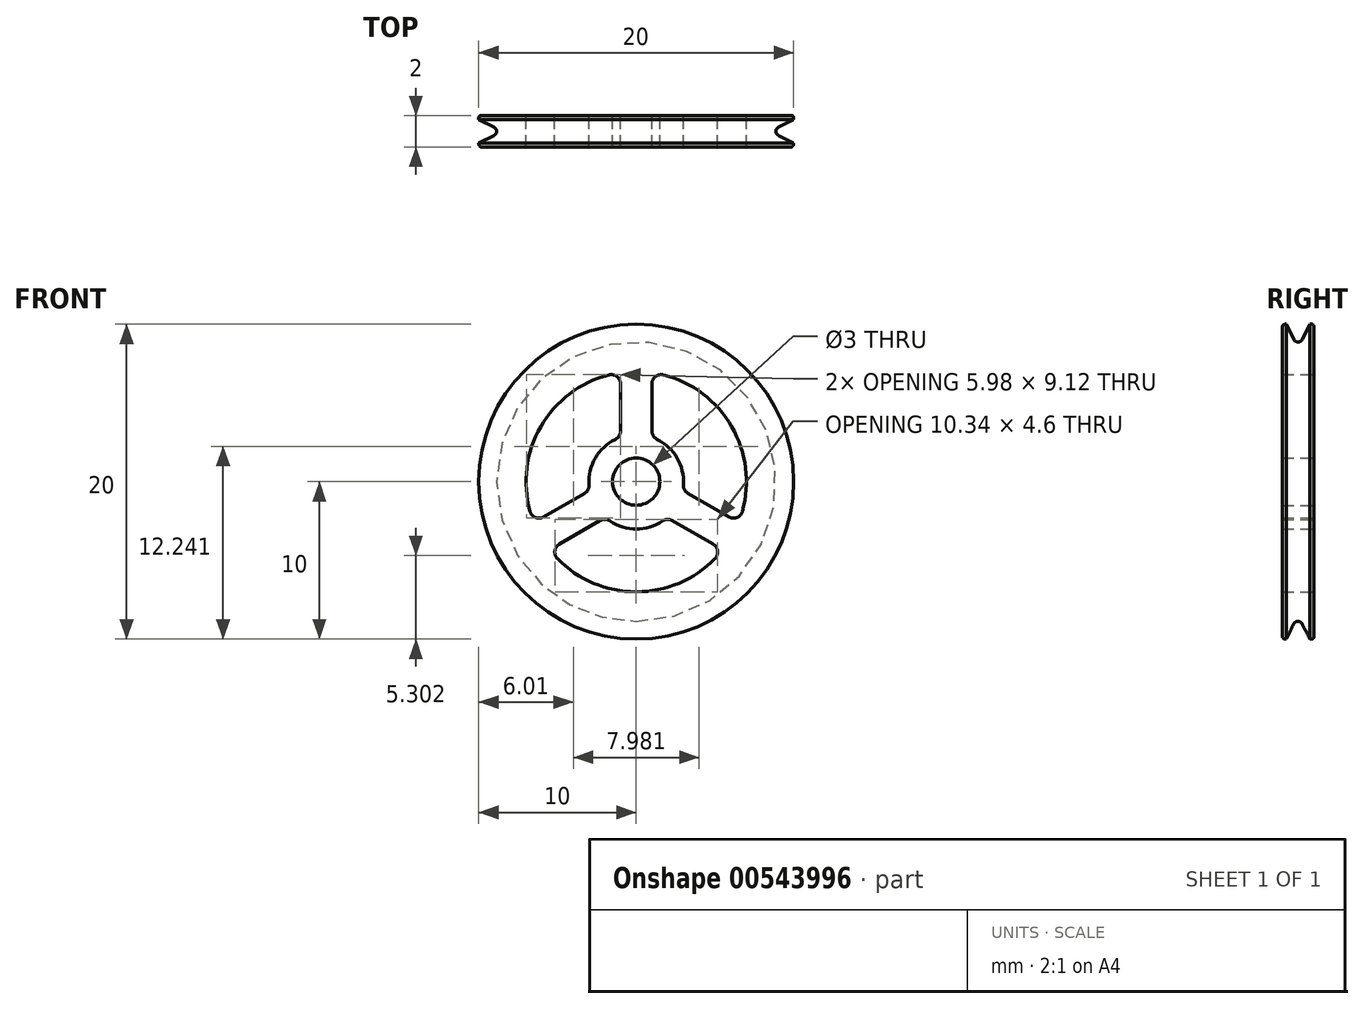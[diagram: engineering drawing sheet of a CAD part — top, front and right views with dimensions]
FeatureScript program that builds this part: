
annotation { "Feature Type Name" : "Feature", "Feature Type Description" : "" }
export const myFeature = defineFeature(function(context is Context, id is Id, definition is map)
    precondition{}
    {
        {
            var Q0;
            Q0=qCreatedBy(makeId("Front.planeOp"),FACE);
            var sketch = newSketch(context, id + "F0", { "sketchPlane" : qUnion([Q0])});
            skCircle(sketch, "E0", {"center": v(0, 0) * mm, "radius": 10 * mm});
            skArc(sketch, "E1.0", {"start": v(-1.73, 6.78) * mm, "mid": v(-6.06, 3.5) * mm, "end": v(-6.74, -1.9) * mm});
            skArc(sketch, "E2", {"start": v(-1.33, 2.7) * mm, "mid": v(-2.6, 1.5) * mm, "end": v(-3, -0.2) * mm});
            skCircle(sketch, "E3", {"center": v(0, 0) * mm, "radius": 1.5 * mm});
            skLineSegment(sketch, "E4.0", {"start": v(-1, 10) * mm, "end": v(-1, 9.95) * mm});
            skLineSegment(sketch, "E5.0", {"start": v(1, 10) * mm, "end": v(1, 9.95) * mm});
            skLineSegment(sketch, "E6.trimOffspring", {"start": v(-1, 6.21) * mm, "end": v(-1, 3.22) * mm});
            skLineSegment(sketch, "E7.trimOffspring", {"start": v(1, 6.21) * mm, "end": v(1, 3.22) * mm});
            skLineSegment(sketch, "E8.1.0", {"start": v(-5.88, -2.24) * mm, "end": v(-3.29, -0.74) * mm});
            skLineSegment(sketch, "E8.1.1", {"start": v(-4.88, -3.97) * mm, "end": v(-2.29, -2.47) * mm});
            skLineSegment(sketch, "E8.2.0", {"start": v(4.88, -3.97) * mm, "end": v(2.29, -2.47) * mm});
            skLineSegment(sketch, "E8.2.1", {"start": v(5.88, -2.24) * mm, "end": v(3.29, -0.74) * mm});
            skArc(sketch, "E9.trimOffspring", {"start": v(6.74, -1.9) * mm, "mid": v(6.06, 3.5) * mm, "end": v(1.73, 6.78) * mm});
            skArc(sketch, "E10.trimOffspring", {"start": v(-5, -4.9) * mm, "mid": v(0, -7) * mm, "end": v(5, -4.9) * mm});
            skArc(sketch, "E11.trimOffspring", {"start": v(3, -0.2) * mm, "mid": v(2.6, 1.5) * mm, "end": v(1.33, 2.7) * mm});
            skArc(sketch, "E12.trimOffspring", {"start": v(-1.67, -2.5) * mm, "mid": v(0, -3) * mm, "end": v(1.67, -2.5) * mm});
            skPoint(sketch, "E13.visualSharp", {"position": v(-1, 6.93) * mm});
            skArc(sketch, "E13.filletArc", {"start": v(-1, 6.21) * mm, "mid": v(-1.23, 6.68) * mm, "end": v(-1.73, 6.78) * mm});
            skPoint(sketch, "E14.visualSharp", {"position": v(-1, 2.83) * mm});
            skArc(sketch, "E14.filletArc", {"start": v(-1.33, 2.7) * mm, "mid": v(-1.09, 2.9) * mm, "end": v(-1, 3.22) * mm});
            skPoint(sketch, "E15.visualSharp", {"position": v(-2.95, -0.55) * mm});
            skArc(sketch, "E15.filletArc", {"start": v(-3.29, -0.74) * mm, "mid": v(-3.06, -0.51) * mm, "end": v(-3, -0.2) * mm});
            skPoint(sketch, "E16.visualSharp", {"position": v(-6.5, -2.6) * mm});
            skArc(sketch, "E16.filletArc", {"start": v(-6.74, -1.9) * mm, "mid": v(-6.4, -2.28) * mm, "end": v(-5.88, -2.24) * mm});
            skPoint(sketch, "E17.visualSharp", {"position": v(1, 6.93) * mm});
            skArc(sketch, "E17.filletArc", {"start": v(1.73, 6.78) * mm, "mid": v(1.23, 6.68) * mm, "end": v(1, 6.21) * mm});
            skPoint(sketch, "E18.visualSharp", {"position": v(6.5, -2.6) * mm});
            skArc(sketch, "E18.filletArc", {"start": v(5.88, -2.24) * mm, "mid": v(6.4, -2.28) * mm, "end": v(6.74, -1.9) * mm});
            skPoint(sketch, "E19.visualSharp", {"position": v(1, 2.83) * mm});
            skArc(sketch, "E19.filletArc", {"start": v(1, 3.22) * mm, "mid": v(1.09, 2.9) * mm, "end": v(1.33, 2.7) * mm});
            skPoint(sketch, "E20.visualSharp", {"position": v(2.95, -0.55) * mm});
            skArc(sketch, "E20.filletArc", {"start": v(3, -0.2) * mm, "mid": v(3.06, -0.51) * mm, "end": v(3.29, -0.74) * mm});
            skPoint(sketch, "E21.visualSharp", {"position": v(5.5, -4.33) * mm});
            skArc(sketch, "E21.filletArc", {"start": v(5, -4.9) * mm, "mid": v(5.17, -4.4) * mm, "end": v(4.88, -3.97) * mm});
            skPoint(sketch, "E22.visualSharp", {"position": v(1.95, -2.28) * mm});
            skArc(sketch, "E22.filletArc", {"start": v(2.29, -2.47) * mm, "mid": v(1.97, -2.4) * mm, "end": v(1.67, -2.5) * mm});
            skPoint(sketch, "E23.visualSharp", {"position": v(-1.95, -2.28) * mm});
            skArc(sketch, "E23.filletArc", {"start": v(-1.67, -2.5) * mm, "mid": v(-1.97, -2.4) * mm, "end": v(-2.29, -2.47) * mm});
            skPoint(sketch, "E24.visualSharp", {"position": v(-5.5, -4.33) * mm});
            skArc(sketch, "E24.filletArc", {"start": v(-4.88, -3.97) * mm, "mid": v(-5.17, -4.4) * mm, "end": v(-5, -4.9) * mm});
            skCircle(sketch, "E25", {"center": v(-4.38, 13.8) * mm, "radius": 3.26 * mm});
            skSolve(sketch);
        }
        {
            var Q0;
            Q0=makeQuery(id+"F0.imprint","IMPRINT",FACE,{"disambiguationData":[TD([[makeQuery(id+"F0.imprint","IMPRINT",EDGE,{"derivedFrom":sQuery(id+"F0.wireOp",EDGE,"E1.0")}),-1.0]])]});
            extrude(context, id + "F1", {"entities" : qUnion([Q0]), "endBound" : BoundingType.SYMMETRIC, "depth" : 2 * mm, "offsetDistance" : 25 * mm});
        }
        {
            var Q0;
            Q0=makeQuery(id+"F1.opExtrude","CAP_EDGE",EDGE,{"disambiguationData":[OSD([sQuery(id+"F0.wireOp",EDGE,"E0")])],"isStart":true});
            fillet(context, id + "F2", {"entities" : qUnion([Q0]), "radius" : 0.12 * mm, "tangentPropagation" : true, "allowEdgeOverflow" : false});
        }
        {
            var Q0;
            Q0=qCreatedBy(makeId("Right.planeOp"),FACE);
            var sketch = newSketch(context, id + "F3", { "sketchPlane" : qUnion([Q0])});
            skLineSegment(sketch, "E26", {"start": v(0, 10) * mm, "end": v(0.75, 10) * mm});
            skLineSegment(sketch, "E27", {"start": v(0.75, 10) * mm, "end": v(0.27, 9.04) * mm});
            skLineSegment(sketch, "E28", {"start": v(0, 8.5) * mm, "end": v(0, 10) * mm});
            skLineSegment(sketch, "E29.MirrorCS", {"start": v(-0.75, 10) * mm, "end": v(-0.27, 9.04) * mm});
            skLineSegment(sketch, "E30.MirrorCS", {"start": v(0, 10) * mm, "end": v(-0.75, 10) * mm});
            skLineSegment(sketch, "E31", {"start": v(6.49, 0) * mm, "end": v(-9.8, 0) * mm, "construction": true});
            skPoint(sketch, "E32.visualSharp", {"position": v(0, 8.5) * mm});
            skArc(sketch, "E32.filletArc", {"start": v(-0.27, 9.04) * mm, "mid": v(0, 8.87) * mm, "end": v(0.27, 9.04) * mm});
            skSolve(sketch);
        }
        {
            var Q0;
            Q0 = qSketchRegion(id + "F3", true);
            var Q1;
            Q1=sQuery(id+"F3.wireOp",EDGE,"E31");
            revolve(context, id + "F4", {"operationType" : NewBodyOperationType.REMOVE, "entities" : qUnion([Q0]), "axis" : qUnion([Q1]), "revolveType" : RevolveType.FULL, "oppositeDirection" : true});
        }
        {
            var Q0;
            Q0=makeQuery(id+"F1.opExtrude","CAP_EDGE",EDGE,{"disambiguationData":[OSD([sQuery(id+"F0.wireOp",EDGE,"E0")])],"isStart":false});
            var Q1;
            Q1=makeQuery(id+"F2.opFillet","BLEND_FACE",FACE,{"disambiguationData":[OSD([sQuery(id+"F0.wireOp",EDGE,"E0")])]});
            fillet(context, id + "F5", {"entities" : qUnion([Q0, Q1]), "radius" : 0.2 * mm, "tangentPropagation" : true, "allowEdgeOverflow" : false});
        }
    });
